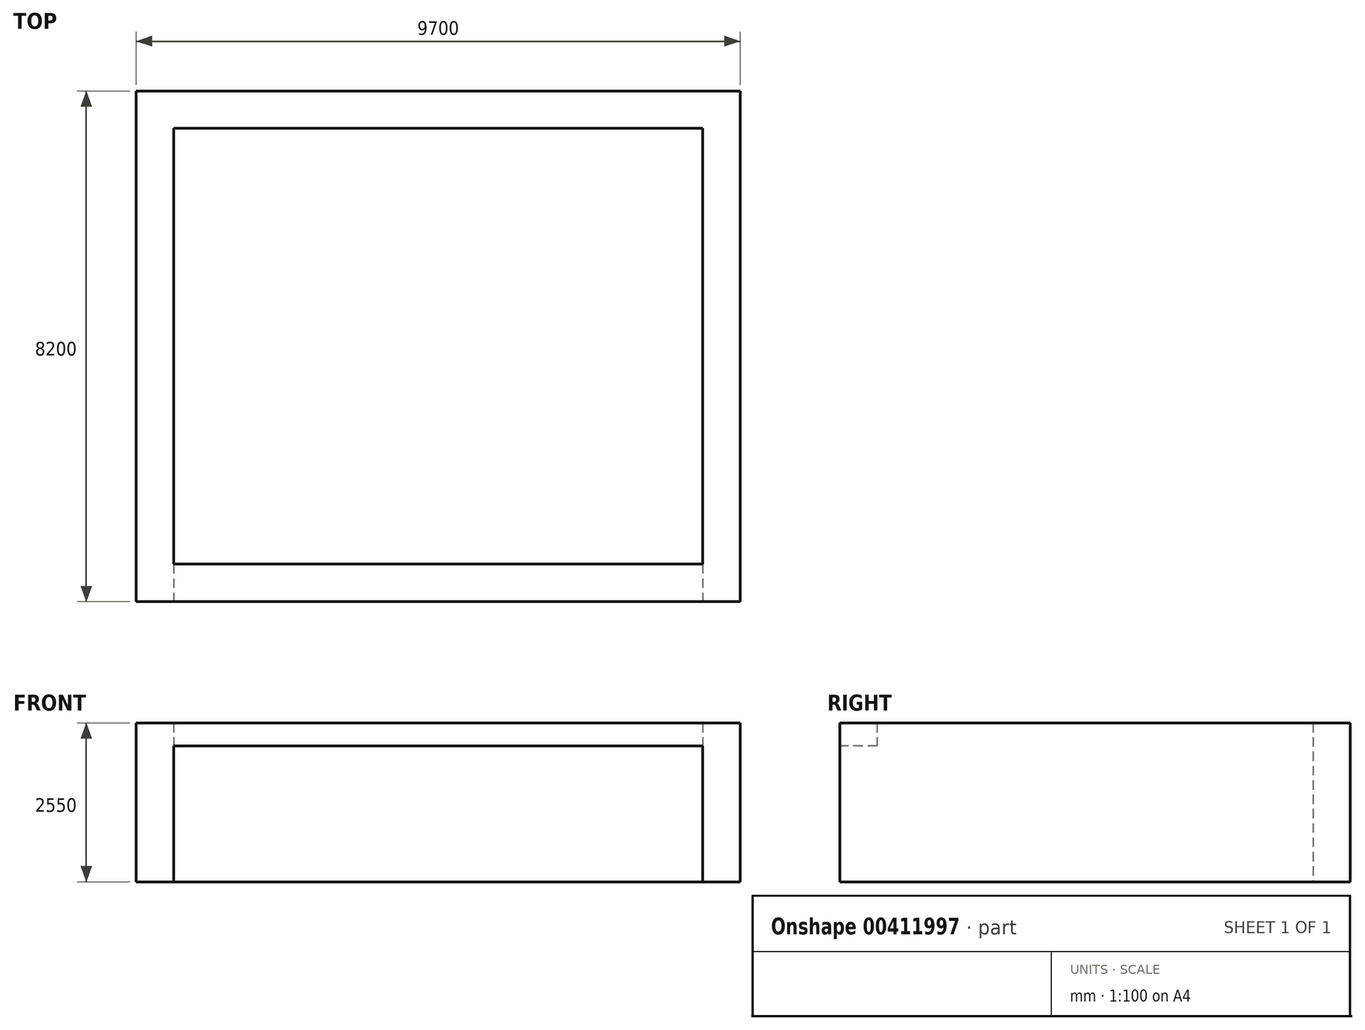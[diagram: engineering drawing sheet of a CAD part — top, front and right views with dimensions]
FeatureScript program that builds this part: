
annotation { "Feature Type Name" : "Feature", "Feature Type Description" : "" }
export const myFeature = defineFeature(function(context is Context, id is Id, definition is map)
    precondition{}
    {
        {
            var Q0;
            Q0=qCreatedBy(makeId("Top.planeOp"),FACE);
            var sketch = newSketch(context, id + "F0", { "sketchPlane" : qUnion([Q0])});
            skLineSegment(sketch, "E0.bottom", {"start": v(8500, 7000) * mm, "end": v(0, 7000) * mm});
            skLineSegment(sketch, "E0.top", {"start": v(8500, 0) * mm, "end": v(0, 0) * mm});
            skLineSegment(sketch, "E0.left", {"start": v(8500, 7000) * mm, "end": v(8500, 0) * mm});
            skLineSegment(sketch, "E0.right", {"start": v(0, 7000) * mm, "end": v(0, 0) * mm});
            skLineSegment(sketch, "E1.bottom", {"start": v(-600, 7600) * mm, "end": v(9100, 7600) * mm});
            skLineSegment(sketch, "E1.top", {"start": v(-600, -600) * mm, "end": v(9100, -600) * mm});
            skLineSegment(sketch, "E1.left", {"start": v(-600, 7600) * mm, "end": v(-600, -600) * mm});
            skLineSegment(sketch, "E1.right", {"start": v(9100, 7600) * mm, "end": v(9100, -600) * mm});
            skSolve(sketch);
        }
        {
            var Q0;
            Q0=qSketchRegion(id+"F0",true);
            extrude(context, id + "F1", {"entities" : qUnion([Q0]), "depth" : 2550 * mm});
        }
        {
            var Q0;
            Q0=makeQuery(id+"F1.opExtrude","SWEPT_FACE",FACE,{"disambiguationData":[OSD([sQuery(id+"F0.wireOp",EDGE,"E1.top")])]});
            var sketch = newSketch(context, id + "F2", { "sketchPlane" : qUnion([Q0])});
            skLineSegment(sketch, "E2.bottom", {"start": v(0, 0) * mm, "end": v(8500, 0) * mm});
            skLineSegment(sketch, "E2.top", {"start": v(0, 2180) * mm, "end": v(8500, 2180) * mm});
            skLineSegment(sketch, "E2.left", {"start": v(0, 0) * mm, "end": v(0, 2180) * mm});
            skLineSegment(sketch, "E2.right", {"start": v(8500, 0) * mm, "end": v(8500, 2180) * mm});
            skSolve(sketch);
        }
        {
            var Q0;
            Q0=qSketchRegion(id+"F2",true);
            var Q1;
            Q1=makeQuery(id+"F1.opExtrude","SWEPT_FACE",FACE,{"disambiguationData":[OSD([sQuery(id+"F0.wireOp",EDGE,"E0.top")])]});
            extrude(context, id + "F3", {"entities" : qUnion([Q0]), "operationType" : NewBodyOperationType.REMOVE, "oppositeDirection" : true, "endBoundEntityFace" : qUnion([Q1]), "depth" : 1000 * mm});
        }
    });
